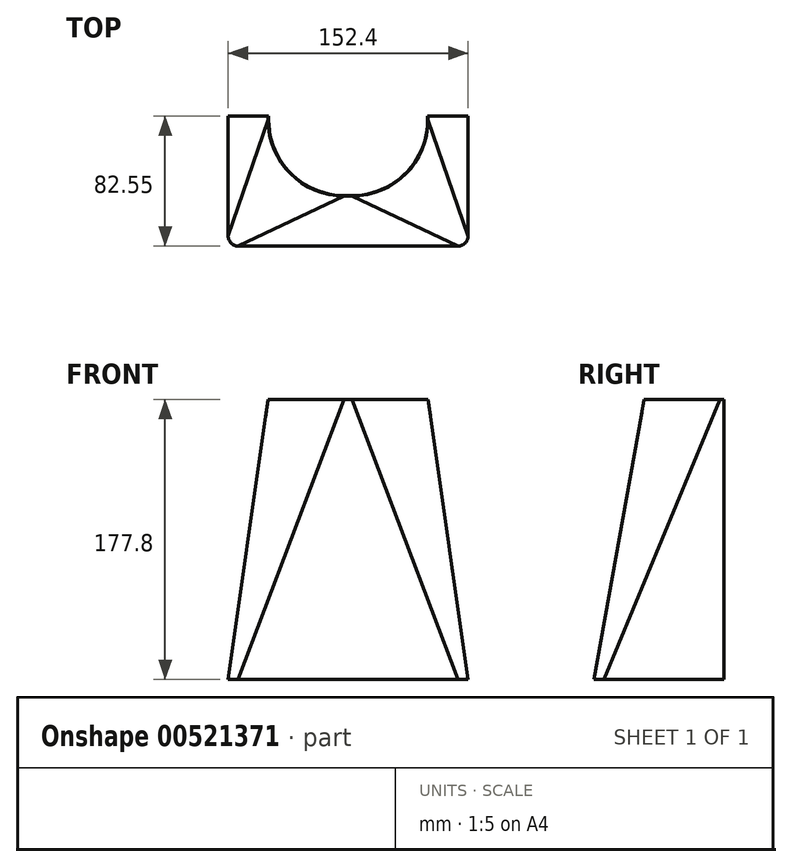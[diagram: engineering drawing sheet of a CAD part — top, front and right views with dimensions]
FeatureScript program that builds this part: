
annotation { "Feature Type Name" : "Feature", "Feature Type Description" : "" }
export const myFeature = defineFeature(function(context is Context, id is Id, definition is map)
    precondition{}
    {
        {
            var Q0;
            Q0=qCreatedBy(makeId("Top.planeOp"),FACE);
            var sketch = newSketch(context, id + "F0", { "sketchPlane" : qUnion([Q0])});
            skLineSegment(sketch, "E0.bottom", {"start": v(69.85, 82.55) * mm, "end": v(-69.85, 82.55) * mm});
            skLineSegment(sketch, "E0.top", {"start": v(69.85, -82.55) * mm, "end": v(-69.85, -82.55) * mm});
            skLineSegment(sketch, "E0.left", {"start": v(76.2, 76.2) * mm, "end": v(76.2, -76.2) * mm});
            skLineSegment(sketch, "E0.right", {"start": v(-76.2, 76.2) * mm, "end": v(-76.2, -76.2) * mm});
            skPoint(sketch, "E0.middle", {"position": v(0, 0) * mm});
            skPoint(sketch, "E1.visualSharp", {"position": v(76.2, -82.55) * mm});
            skArc(sketch, "E1.filletArc", {"start": v(69.85, -82.55) * mm, "mid": v(74.34, -80.7) * mm, "end": v(76.2, -76.2) * mm});
            skPoint(sketch, "E2.visualSharp", {"position": v(76.2, 82.55) * mm});
            skArc(sketch, "E2.filletArc", {"start": v(76.2, 76.2) * mm, "mid": v(74.34, 80.7) * mm, "end": v(69.85, 82.55) * mm});
            skPoint(sketch, "E3.visualSharp", {"position": v(-76.2, 82.55) * mm});
            skArc(sketch, "E3.filletArc", {"start": v(-69.85, 82.55) * mm, "mid": v(-74.34, 80.7) * mm, "end": v(-76.2, 76.2) * mm});
            skPoint(sketch, "E4.visualSharp", {"position": v(-76.2, -82.55) * mm});
            skArc(sketch, "E4.filletArc", {"start": v(-76.2, -76.2) * mm, "mid": v(-74.34, -80.7) * mm, "end": v(-69.85, -82.55) * mm});
            skSolve(sketch);
        }
        {
            var Q0;
            Q0=qCreatedBy(makeId("Top.planeOp"),FACE);
            cPlane(context, id + "F1", {"entities" : qUnion([Q0]), "cplaneType" : CPlaneType.OFFSET, "offset" : 177.8 * mm, "width" : 152.4 * mm, "height" : 152.4 * mm});
        }
        {
            var Q0;
            Q0=qCreatedBy(id+"F1.planeOp",FACE);
            var sketch = newSketch(context, id + "F2", { "sketchPlane" : qUnion([Q0])});
            skCircle(sketch, "E5", {"center": v(0, 0) * mm, "radius": 50.8 * mm, "construction": true});
            skLineSegment(sketch, "E6.bottom", {"start": v(2.54, 50.8) * mm, "end": v(-2.54, 50.8) * mm});
            skLineSegment(sketch, "E6.top", {"start": v(2.54, -50.8) * mm, "end": v(-2.54, -50.8) * mm});
            skLineSegment(sketch, "E6.left", {"start": v(50.8, 2.54) * mm, "end": v(50.8, -2.54) * mm});
            skLineSegment(sketch, "E6.right", {"start": v(-50.8, 2.54) * mm, "end": v(-50.8, -2.54) * mm});
            skPoint(sketch, "E7.visualSharp", {"position": v(-50.8, 50.8) * mm});
            skArc(sketch, "E7.filletArc", {"start": v(-2.54, 50.8) * mm, "mid": v(-36.66, 36.66) * mm, "end": v(-50.8, 2.54) * mm});
            skPoint(sketch, "E8.visualSharp", {"position": v(50.8, 50.8) * mm});
            skArc(sketch, "E8.filletArc", {"start": v(50.8, 2.54) * mm, "mid": v(36.66, 36.66) * mm, "end": v(2.54, 50.8) * mm});
            skPoint(sketch, "E9.visualSharp", {"position": v(50.8, -50.8) * mm});
            skArc(sketch, "E9.filletArc", {"start": v(2.54, -50.8) * mm, "mid": v(36.66, -36.66) * mm, "end": v(50.8, -2.54) * mm});
            skPoint(sketch, "E10.visualSharp", {"position": v(-50.8, -50.8) * mm});
            skArc(sketch, "E10.filletArc", {"start": v(-50.8, -2.54) * mm, "mid": v(-36.66, -36.66) * mm, "end": v(-2.54, -50.8) * mm});
            skSolve(sketch);
        }
        {
            var Q0;
            Q0 = qSketchRegion(id + "F0", true);
            var Q1;
            Q1 = qSketchRegion(id + "F2", true);
            var Q2;
            Q2 = qConstructionFilter(qBodyType(qCreatedBy(id + "F0" ,EDGE), BodyType.WIRE), ConstructionObject.NO);
            var Q3;
            Q3 = qConstructionFilter(qBodyType(qCreatedBy(id + "F2" ,EDGE), BodyType.WIRE), ConstructionObject.NO);
            loft(context, id + "F3", {"sheetProfilesArray" : [{ "sheetProfileEntities" : qUnion([Q0]) }, { "sheetProfileEntities" : qUnion([Q1]) }], "wireProfilesArray" : [{ "wireProfileEntities" : qUnion([Q2]) }, { "wireProfileEntities" : qUnion([Q3]) }]});
        }
        {
            var Q0;
            Q0=qCreatedBy(makeId("Front.planeOp"),FACE);
            var sketch = newSketch(context, id + "F4", { "sketchPlane" : qUnion([Q0])});
            skLineSegment(sketch, "E11.bottom", {"start": v(114.3, 177.8) * mm, "end": v(-114.3, 177.8) * mm});
            skLineSegment(sketch, "E11.top", {"start": v(114.3, 0) * mm, "end": v(-114.3, 0) * mm});
            skLineSegment(sketch, "E11.left", {"start": v(114.3, 177.8) * mm, "end": v(114.3, 0) * mm});
            skLineSegment(sketch, "E11.right", {"start": v(-114.3, 177.8) * mm, "end": v(-114.3, 0) * mm});
            skPoint(sketch, "E11.middle", {"position": v(0, 88.9) * mm});
            skSolve(sketch);
        }
        {
            var Q0;
            Q0 = qSketchRegion(id + "F4", true);
            extrude(context, id + "F5", {"entities" : qUnion([Q0]), "operationType" : NewBodyOperationType.REMOVE, "endBound" : BoundingType.THROUGH_ALL, "oppositeDirection" : true, "depth" : 25.4 * mm, "offsetDistance" : 25.4 * mm});
        }
        {
            var Q0;
            Q0=makeQuery(id+"F3.opLoft","CAP_FACE",FACE,{"disambiguationData":[OSD([makeQuery(id+"F2.imprint","IMPRINT",FACE,{"disambiguationData":[TD([[makeQuery(id+"F2.imprint","IMPRINT",EDGE,{"derivedFrom":sQuery(id+"F2.wireOp",EDGE,"E6.bottom")}),1.0]])]})])],"isStart":true});
            var Q1;
            Q1=makeQuery(id+"F5.boolean.opBoolean","COPY",FACE,{"derivedFrom":makeQuery(id+"F5.opExtrude","CAP_FACE",FACE,{"disambiguationData":[OSD([sQuery(id+"F4.wireOp",EDGE,"E11.bottom"),sQuery(id+"F4.wireOp",EDGE,"E11.top"),sQuery(id+"F4.wireOp",EDGE,"E11.left"),sQuery(id+"F4.wireOp",EDGE,"E11.right")])],"isStart":true})});
            var Q2;
            Q2=makeQuery(id+"F3.opLoft","CAP_FACE",FACE,{"disambiguationData":[OSD([makeQuery(id+"F0.imprint","IMPRINT",FACE,{"disambiguationData":[TD([[makeQuery(id+"F0.imprint","IMPRINT",EDGE,{"derivedFrom":sQuery(id+"F0.wireOp",EDGE,"E0.bottom")}),1.0]])]})])],"isStart":true});
            shell(context, id + "F6", {"entities" : qUnion([Q0, Q1, Q2]), "thickness" : 0.32 * mm});
        }
    });
